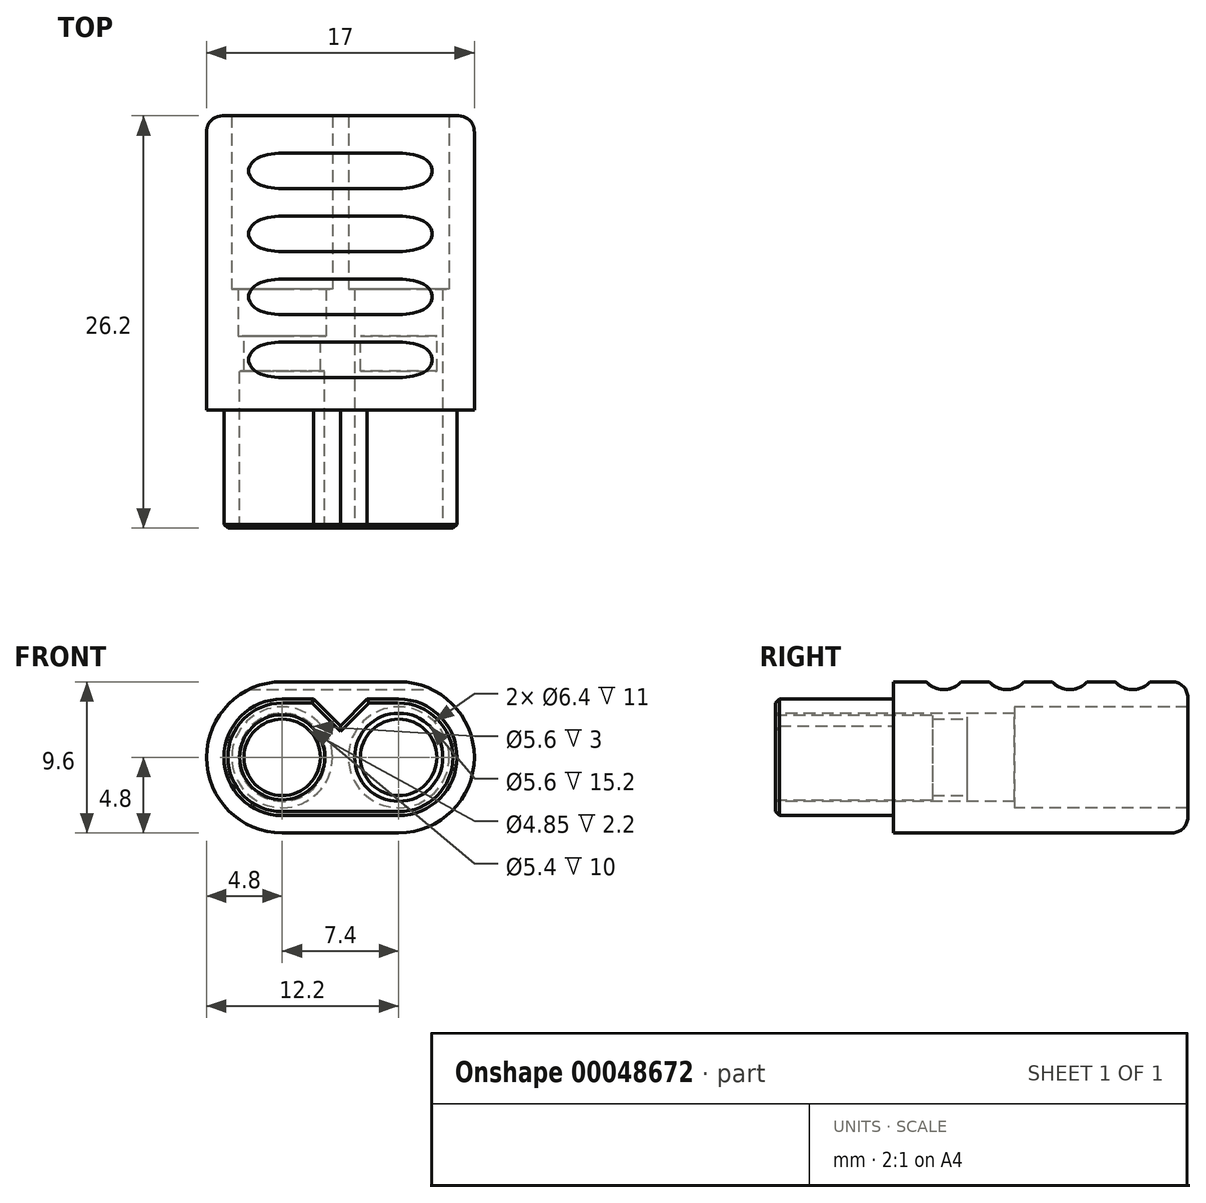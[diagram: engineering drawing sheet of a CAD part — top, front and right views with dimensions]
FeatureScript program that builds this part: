
annotation { "Feature Type Name" : "Feature", "Feature Type Description" : "" }
export const myFeature = defineFeature(function(context is Context, id is Id, definition is map)
    precondition{}
    {
        {
            var Q0;
            Q0=qCreatedBy(makeId("Front.planeOp"),FACE);
            var sketch = newSketch(context, id + "F0", { "sketchPlane" : qUnion([Q0])});
            skCircle(sketch, "E0", {"center": v(-3.7, 0) * mm, "radius": 2.43 * mm});
            skCircle(sketch, "E1.MirrorC", {"center": v(-3.7, 0) * mm, "radius": 2.8 * mm});
            skLineSegment(sketch, "E2", {"start": v(0, 0) * mm, "end": v(-8.5, 0) * mm, "construction": true});
            skArc(sketch, "E3", {"start": v(-3.7, 4.8) * mm, "mid": v(-7.1, 3.4) * mm, "end": v(-8.5, 0) * mm});
            skLineSegment(sketch, "E4", {"start": v(0, 4.8) * mm, "end": v(0, 0) * mm, "construction": true});
            skLineSegment(sketch, "E5", {"start": v(-3.7, 4.8) * mm, "end": v(-3.7, 0) * mm, "construction": true});
            skCircle(sketch, "E6.MirrorC", {"center": v(3.7, 0) * mm, "radius": 2.43 * mm});
            skCircle(sketch, "E7.MirrorC", {"center": v(3.7, 0) * mm, "radius": 2.8 * mm});
            skLineSegment(sketch, "E8", {"start": v(-3.7, 4.8) * mm, "end": v(0, 4.8) * mm});
            skArc(sketch, "E9.MirrorCS", {"start": v(-3.7, -4.8) * mm, "mid": v(-7.1, -3.4) * mm, "end": v(-8.5, 0) * mm});
            skLineSegment(sketch, "E10.MirrorCS", {"start": v(-3.7, -4.8) * mm, "end": v(0, -4.8) * mm});
            skLineSegment(sketch, "E11.MirrorCS", {"start": v(3.7, 4.8) * mm, "end": v(0, 4.8) * mm});
            skArc(sketch, "E12.MirrorCS", {"start": v(3.7, 4.8) * mm, "mid": v(7.1, 3.4) * mm, "end": v(8.5, 0) * mm});
            skArc(sketch, "E13.MirrorCS", {"start": v(3.7, -4.8) * mm, "mid": v(7.1, -3.4) * mm, "end": v(8.5, 0) * mm});
            skLineSegment(sketch, "E14.MirrorCS", {"start": v(3.7, -4.8) * mm, "end": v(0, -4.8) * mm});
            skSolve(sketch);
        }
        {
            var Q0;
            Q0=makeQuery(id+"F0.imprint","IMPRINT",FACE,{"disambiguationData":[TD([[makeQuery(id+"F0.imprint","IMPRINT",EDGE,{"derivedFrom":sQuery(id+"F0.wireOp",EDGE,"E1.MirrorC")}),-1.0]])]});
            extrude(context, id + "F1", {"entities" : qUnion([Q0]), "oppositeDirection" : true, "depth" : 3 * mm});
        }
        {
            var Q0;
            Q0=makeQuery(id+"F0.imprint","IMPRINT",FACE,{"disambiguationData":[TD([[makeQuery(id+"F0.imprint","IMPRINT",EDGE,{"derivedFrom":sQuery(id+"F0.wireOp",EDGE,"E1.MirrorC")}),-1.0]])]});
            var Q1;
            Q1=makeQuery(id+"F0.imprint","IMPRINT",FACE,{"disambiguationData":[TD([[makeQuery(id+"F0.imprint","IMPRINT",EDGE,{"derivedFrom":sQuery(id+"F0.wireOp",EDGE,"E0")}),-1.0]])]});
            var Q2;
            Q2=makeQuery(id+"F0.imprint","IMPRINT",FACE,{"disambiguationData":[TD([[makeQuery(id+"F0.imprint","IMPRINT",EDGE,{"derivedFrom":sQuery(id+"F0.wireOp",EDGE,"E6.MirrorC")}),1.0]])]});
            extrude(context, id + "F2", {"entities" : qUnion([Q0, Q1, Q2]), "operationType" : NewBodyOperationType.ADD, "depth" : 2.2 * mm});
        }
        {
            var Q0;
            Q0=makeQuery(id+"F2.opExtrude","CAP_FACE",FACE,{"disambiguationData":[OSD([sQuery(id+"F0.wireOp",EDGE,"9af29b95-2ce9-48ef-83fd-eb93086e848a.bottom"),sQuery(id+"F0.wireOp",EDGE,"9af29b95-2ce9-48ef-83fd-eb93086e848a.top"),sQuery(id+"F0.wireOp",EDGE,"9af29b95-2ce9-48ef-83fd-eb93086e848a.left"),sQuery(id+"F0.wireOp",EDGE,"9af29b95-2ce9-48ef-83fd-eb93086e848a.right"),sQuery(id+"F0.wireOp",EDGE,"E0"),sQuery(id+"F0.wireOp",EDGE,"3bfeefd6-8ccf-4d28-93f8-2f2611132b7e0.MirrorC")])],"isStart":false});
            var sketch = newSketch(context, id + "F3", { "sketchPlane" : qUnion([Q0])});
            skCircle(sketch, "E15", {"center": v(-3.7, 0) * mm, "radius": 2.7 * mm});
            skCircle(sketch, "E16.MirrorC", {"center": v(3.7, 0) * mm, "radius": 2.7 * mm});
            skSolve(sketch);
        }
        {
            var Q0;
            Q0=makeQuery(id+"F3.imprint","IMPRINT",FACE,{"disambiguationData":[TD([[makeQuery(id+"F3.imprint","IMPRINT",EDGE,{"derivedFrom":sQuery(id+"F3.wireOp",EDGE,"E15")}),-1.0]])]});
            extrude(context, id + "F4", {"entities" : qUnion([Q0]), "operationType" : NewBodyOperationType.ADD, "depth" : 2.5 * mm});
        }
        {
            var Q0;
            Q0=makeQuery(id+"F4.opExtrude","CAP_FACE",FACE,{"disambiguationData":[OSD([sQuery(id+"F0.wireOp",EDGE,"6d7ef5f6-68e2-491c-bdb9-d34946de3217"),sQuery(id+"F0.wireOp",EDGE,"4a62e17a-e464-4ae6-85fd-e67879230d62"),sQuery(id+"F0.wireOp",EDGE,"d8da9cf0-fa24-4876-8edd-ab64fd6ac28d"),sQuery(id+"F0.wireOp",EDGE,"6ed2982d-5885-44c9-aeb3-c63c06cbabe1.filletArc"),sQuery(id+"F0.wireOp",EDGE,"ac0d3ca8-c71e-4b4c-905e-2867e2134c0f.filletArc"),sQuery(id+"F0.wireOp",EDGE,"db059e13-4987-40d7-b22c-4aa99c86301e0.MirrorCS"),sQuery(id+"F0.wireOp",EDGE,"21968229-6fcb-4818-9fba-464d6f3a7a490.MirrorCS"),sQuery(id+"F0.wireOp",EDGE,"27c3a9c7-bba5-4ce6-a0b2-ee3fde2fc81d0.MirrorCS"),sQuery(id+"F0.wireOp",EDGE,"74e78b0a-03c2-4682-ad69-f2b08288fff30.MirrorCS"),sQuery(id+"F0.wireOp",EDGE,"d6014dcf-48b1-47f5-9b02-8fcda7855cd30.MirrorCS"),sQuery(id+"F3.wireOp",EDGE,"E15"),sQuery(id+"F3.wireOp",EDGE,"3893830b-eff6-4bac-9637-d990255e7b810.MirrorC")])],"isStart":false});
            var sketch = newSketch(context, id + "F5", { "sketchPlane" : qUnion([Q0])});
            skLineSegment(sketch, "E17", {"start": v(-3.7, -3.7) * mm, "end": v(0, -3.7) * mm});
            skLineSegment(sketch, "E18", {"start": v(-1.7, 3.7) * mm, "end": v(0, 2) * mm});
            skArc(sketch, "E19", {"start": v(-3.7, 3.7) * mm, "mid": v(-7.4, 0) * mm, "end": v(-3.7, -3.7) * mm});
            skLineSegment(sketch, "E20", {"start": v(-3.7, 3.7) * mm, "end": v(-1.7, 3.7) * mm});
            skLineSegment(sketch, "E21.MirrorCS", {"start": v(1.7, 3.7) * mm, "end": v(0, 2) * mm});
            skLineSegment(sketch, "E22.MirrorCS", {"start": v(3.7, 3.7) * mm, "end": v(1.7, 3.7) * mm});
            skArc(sketch, "E23.MirrorCS", {"start": v(3.7, 3.7) * mm, "mid": v(7.4, 0) * mm, "end": v(3.7, -3.7) * mm});
            skLineSegment(sketch, "E24.MirrorCS", {"start": v(3.7, -3.7) * mm, "end": v(0, -3.7) * mm});
            skSolve(sketch);
        }
        {
            var Q0;
            Q0=makeQuery(id+"F5.imprint","IMPRINT",FACE,{"disambiguationData":[TD([[makeQuery(id+"F5.imprint","IMPRINT",EDGE,{"derivedFrom":sQuery(id+"F5.wireOp",EDGE,"dbc5b547-12d9-4310-99b7-08f169881b62")}),1.0]])]});
            var Q1;
            Q1=makeQuery(id+"F5.imprint","IMPRINT",FACE,{"disambiguationData":[TD([[makeQuery(id+"F5.imprint","IMPRINT",EDGE,{"derivedFrom":sQuery(id+"F5.wireOp",EDGE,"E17")}),1.0]])]});
            extrude(context, id + "F6", {"entities" : qUnion([Q0, Q1]), "operationType" : NewBodyOperationType.ADD, "depth" : 7.5 * mm});
        }
        {
            var Q0;
            Q0=makeQuery(id+"F1.opExtrude","CAP_FACE",FACE,{"disambiguationData":[OSD([sQuery(id+"F0.wireOp",EDGE,"E1.MirrorC"),sQuery(id+"F0.wireOp",EDGE,"E3"),sQuery(id+"F0.wireOp",EDGE,"E7.MirrorC"),sQuery(id+"F0.wireOp",EDGE,"E8"),sQuery(id+"F0.wireOp",EDGE,"E9.MirrorCS"),sQuery(id+"F0.wireOp",EDGE,"E10.MirrorCS"),sQuery(id+"F0.wireOp",EDGE,"E11.MirrorCS"),sQuery(id+"F0.wireOp",EDGE,"E12.MirrorCS"),sQuery(id+"F0.wireOp",EDGE,"E13.MirrorCS"),sQuery(id+"F0.wireOp",EDGE,"E14.MirrorCS")])],"isStart":false});
            var sketch = newSketch(context, id + "F7", { "sketchPlane" : qUnion([Q0])});
            skCircle(sketch, "E25", {"center": v(3.7, 0) * mm, "radius": 3.2 * mm});
            skCircle(sketch, "E26.MirrorC", {"center": v(-3.7, 0) * mm, "radius": 3.2 * mm});
            skSolve(sketch);
        }
        {
            var Q0;
            Q0=makeQuery(id+"F7.imprint","IMPRINT",FACE,{"disambiguationData":[TD([[makeQuery(id+"F7.imprint","IMPRINT",EDGE,{"derivedFrom":sQuery(id+"F7.wireOp",EDGE,"E25")}),-1.0]])]});
            extrude(context, id + "F8", {"entities" : qUnion([Q0]), "operationType" : NewBodyOperationType.ADD, "depth" : 11 * mm});
        }
        {
            var Q0;
            Q0=makeQuery(id+"F8.opExtrude","CAP_EDGE",EDGE,{"disambiguationData":[OSD([sQuery(id+"F0.wireOp",EDGE,"E8"),sQuery(id+"F0.wireOp",EDGE,"E11.MirrorCS")])],"isStart":false});
            fillet(context, id + "F9", {"entities" : qUnion([Q0]), "radius" : 1 * mm, "tangentPropagation" : true, "allowEdgeOverflow" : false});
        }
        {
            var Q0;
            Q0=makeQuery(id+"F6.opExtrude","CAP_EDGE",EDGE,{"disambiguationData":[OSD([sQuery(id+"F5.wireOp",EDGE,"E20")])],"isStart":false});
            var Q1;
            Q1=makeQuery(id+"F6.opExtrude","CAP_EDGE",EDGE,{"disambiguationData":[OSD([sQuery(id+"F5.wireOp",EDGE,"E18")])],"isStart":false});
            var Q2;
            Q2=makeQuery(id+"F6.opExtrude","CAP_EDGE",EDGE,{"disambiguationData":[OSD([sQuery(id+"F5.wireOp",EDGE,"E21.MirrorCS")])],"isStart":false});
            chamfer(context, id + "F10", {"entities" : qUnion([Q0, Q1, Q2]), "width" : 0.25 * mm, "tangentPropagation" : true});
        }
        {
            var Q0;
            Q0=qCreatedBy(makeId("Right.planeOp"),FACE);
            var sketch = newSketch(context, id + "F11", { "sketchPlane" : qUnion([Q0])});
            skCircle(sketch, "E27", {"center": v(2.5, 5.8) * mm, "radius": 1.5 * mm});
            skCircle(sketch, "E28", {"center": v(10.5, 5.8) * mm, "radius": 1.5 * mm});
            skLineSegment(sketch, "E29", {"start": v(14.5, 0) * mm, "end": v(-12.5, 0) * mm, "construction": true});
            skCircle(sketch, "E30", {"center": v(6.5, 5.8) * mm, "radius": 1.5 * mm});
            skCircle(sketch, "E31.MirrorC", {"center": v(2.5, -5.8) * mm, "radius": 1.5 * mm});
            skCircle(sketch, "E32.MirrorC", {"center": v(6.5, -5.8) * mm, "radius": 1.5 * mm});
            skCircle(sketch, "E33.MirrorC", {"center": v(10.5, -5.8) * mm, "radius": 1.5 * mm});
            skLineSegment(sketch, "E34", {"start": v(10.5, 5.8) * mm, "end": v(-1.5, 5.8) * mm, "construction": true});
            skCircle(sketch, "E35", {"center": v(-1.5, 5.8) * mm, "radius": 1.5 * mm});
            skCircle(sketch, "E36.MirrorC", {"center": v(-1.5, -5.8) * mm, "radius": 1.5 * mm});
            skSolve(sketch);
        }
        {
            var Q0;
            Q0=makeQuery(id+"F11.imprint","IMPRINT",FACE,{"disambiguationData":[TD([[makeQuery(id+"F11.imprint","IMPRINT",EDGE,{"derivedFrom":sQuery(id+"F11.wireOp",EDGE,"E30")}),1.0]])]});
            var Q1;
            Q1=makeQuery(id+"F11.imprint","IMPRINT",FACE,{"disambiguationData":[TD([[makeQuery(id+"F11.imprint","IMPRINT",EDGE,{"derivedFrom":sQuery(id+"F11.wireOp",EDGE,"E27")}),1.0]])]});
            var Q2;
            Q2=makeQuery(id+"F11.imprint","IMPRINT",FACE,{"disambiguationData":[TD([[makeQuery(id+"F11.imprint","IMPRINT",EDGE,{"derivedFrom":sQuery(id+"F11.wireOp",EDGE,"E31.MirrorC")}),-1.0]])]});
            var Q3;
            Q3=makeQuery(id+"F11.imprint","IMPRINT",FACE,{"disambiguationData":[TD([[makeQuery(id+"F11.imprint","IMPRINT",EDGE,{"derivedFrom":sQuery(id+"F11.wireOp",EDGE,"E32.MirrorC")}),-1.0]])]});
            var Q4;
            Q4=makeQuery(id+"F11.imprint","IMPRINT",FACE,{"disambiguationData":[TD([[makeQuery(id+"F11.imprint","IMPRINT",EDGE,{"derivedFrom":sQuery(id+"F11.wireOp",EDGE,"E33.MirrorC")}),-1.0]])]});
            var Q5;
            Q5=makeQuery(id+"F11.imprint","IMPRINT",FACE,{"disambiguationData":[TD([[makeQuery(id+"F11.imprint","IMPRINT",EDGE,{"derivedFrom":sQuery(id+"F11.wireOp",EDGE,"E28")}),1.0]])]});
            var Q6;
            Q6=makeQuery(id+"F11.imprint","IMPRINT",FACE,{"disambiguationData":[TD([[makeQuery(id+"F11.imprint","IMPRINT",EDGE,{"derivedFrom":sQuery(id+"F11.wireOp",EDGE,"E35")}),1.0]])]});
            var Q7;
            Q7=makeQuery(id+"F11.imprint","IMPRINT",FACE,{"disambiguationData":[TD([[makeQuery(id+"F11.imprint","IMPRINT",EDGE,{"derivedFrom":sQuery(id+"F11.wireOp",EDGE,"E36.MirrorC")}),-1.0]])]});
            extrude(context, id + "F12", {"entities" : qUnion([Q0, Q1, Q2, Q3, Q4, Q5, Q6, Q7]), "operationType" : NewBodyOperationType.REMOVE, "endBound" : BoundingType.SYMMETRIC, "oppositeDirection" : true, "depth" : 17 * mm});
        }
    });
